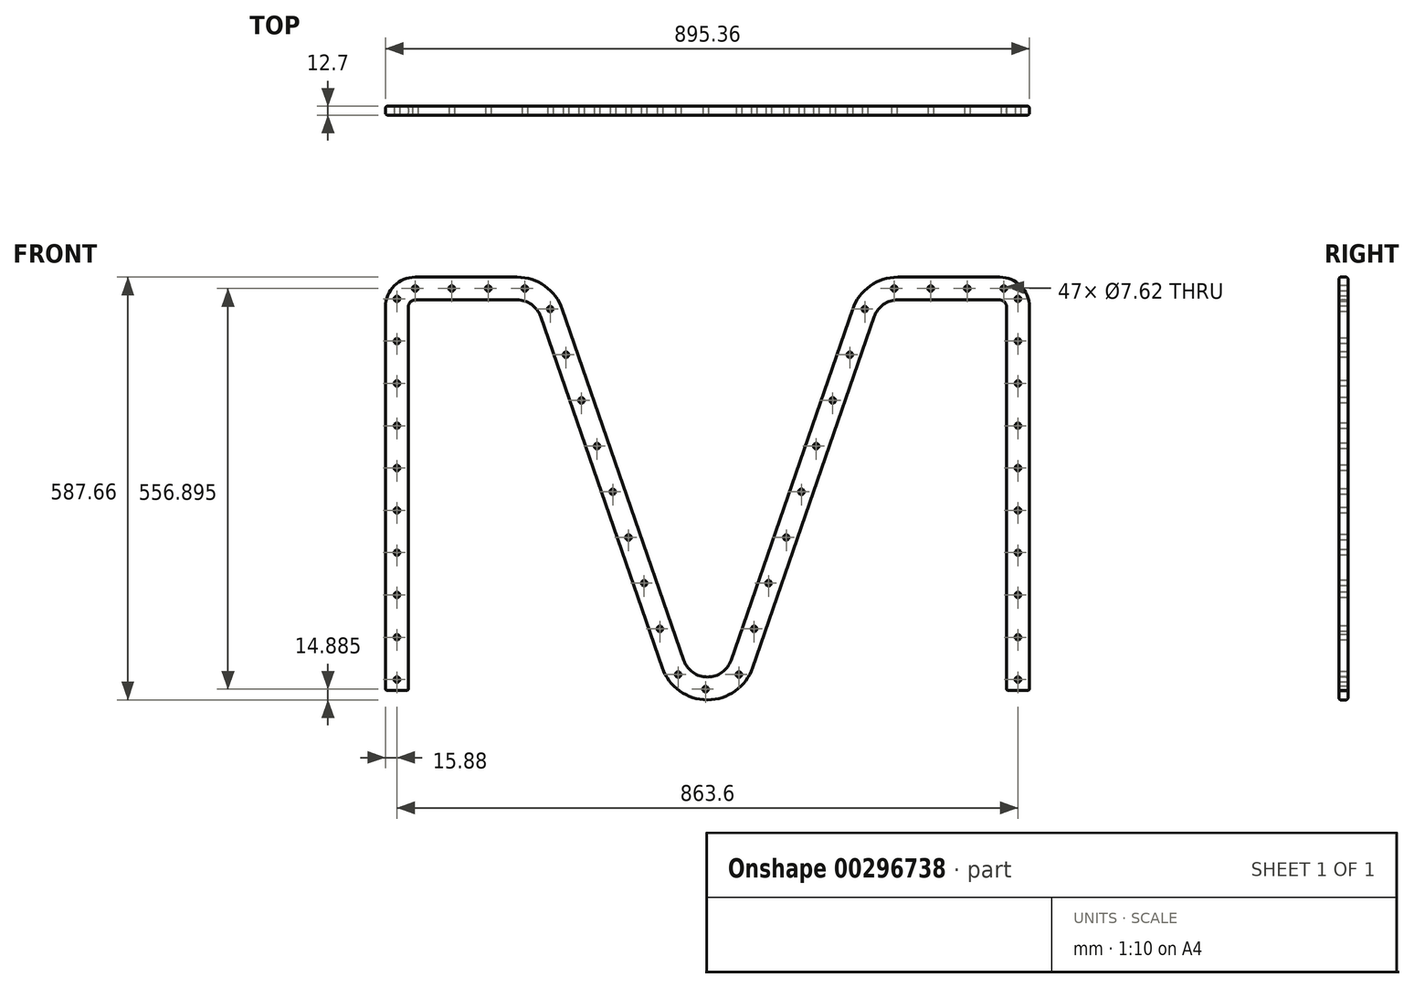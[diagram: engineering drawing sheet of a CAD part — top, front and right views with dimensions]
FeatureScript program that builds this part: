
annotation { "Feature Type Name" : "Feature", "Feature Type Description" : "" }
export const myFeature = defineFeature(function(context is Context, id is Id, definition is map)
    precondition{}
    {
        {
            var Q0;
            Q0=qCreatedBy(makeId("Front.planeOp"),FACE);
            var sketch = newSketch(context, id + "F0", { "sketchPlane" : qUnion([Q0])});
            skLineSegment(sketch, "E0", {"start": v(0, 0) * mm, "end": v(0, 533.4) * mm});
            skLineSegment(sketch, "E1", {"start": v(25.4, 558.8) * mm, "end": v(167.03, 558.8) * mm});
            skLineSegment(sketch, "E2", {"start": v(215.03, 524.62) * mm, "end": v(383.8, 37.08) * mm});
            skLineSegment(sketch, "E3", {"start": v(479.8, 37.08) * mm, "end": v(648.57, 524.62) * mm});
            skLineSegment(sketch, "E4", {"start": v(696.57, 558.8) * mm, "end": v(838.2, 558.8) * mm});
            skLineSegment(sketch, "E5", {"start": v(863.6, 533.4) * mm, "end": v(863.6, 0) * mm});
            skPoint(sketch, "E6.visualSharp", {"position": v(0, 558.8) * mm});
            skArc(sketch, "E6.filletArc", {"start": v(25.4, 558.8) * mm, "mid": v(7.44, 551.36) * mm, "end": v(0, 533.4) * mm});
            skPoint(sketch, "E7.visualSharp", {"position": v(203.2, 558.8) * mm});
            skArc(sketch, "E7.filletArc", {"start": v(215.03, 524.62) * mm, "mid": v(196.5, 549.38) * mm, "end": v(167.03, 558.8) * mm});
            skPoint(sketch, "E8.visualSharp", {"position": v(660.4, 558.8) * mm});
            skArc(sketch, "E8.filletArc", {"start": v(696.57, 558.8) * mm, "mid": v(667.1, 549.38) * mm, "end": v(648.57, 524.62) * mm});
            skPoint(sketch, "E9.visualSharp", {"position": v(431.8, -101.6) * mm});
            skArc(sketch, "E9.filletArc", {"start": v(383.8, 37.08) * mm, "mid": v(431.8, 2.9) * mm, "end": v(479.8, 37.08) * mm});
            skPoint(sketch, "E10.visualSharp", {"position": v(863.6, 558.8) * mm});
            skArc(sketch, "E10.filletArc", {"start": v(863.6, 533.4) * mm, "mid": v(856.16, 551.36) * mm, "end": v(838.2, 558.8) * mm});
            skSolve(sketch);
        }
        {
            var Q0;
            Q0=qCreatedBy(makeId("Top.planeOp"),FACE);
            var sketch = newSketch(context, id + "F1", { "sketchPlane" : qUnion([Q0])});
            skLineSegment(sketch, "E11.bottom", {"start": v(-12.7, 6.35) * mm, "end": v(12.7, 6.35) * mm});
            skLineSegment(sketch, "E11.top", {"start": v(-12.7, -6.35) * mm, "end": v(12.7, -6.35) * mm});
            skLineSegment(sketch, "E11.left", {"start": v(-15.88, 3.18) * mm, "end": v(-15.88, -3.17) * mm});
            skLineSegment(sketch, "E11.right", {"start": v(15.88, 3.18) * mm, "end": v(15.88, -3.17) * mm});
            skPoint(sketch, "E12.visualSharp", {"position": v(-15.88, 6.35) * mm});
            skArc(sketch, "E12.filletArc", {"start": v(-12.7, 6.35) * mm, "mid": v(-14.95, 5.42) * mm, "end": v(-15.88, 3.18) * mm});
            skPoint(sketch, "E13.visualSharp", {"position": v(-15.88, -6.35) * mm});
            skArc(sketch, "E13.filletArc", {"start": v(-15.88, -3.18) * mm, "mid": v(-14.95, -5.42) * mm, "end": v(-12.7, -6.35) * mm});
            skPoint(sketch, "E14.visualSharp", {"position": v(15.88, 6.35) * mm});
            skArc(sketch, "E14.filletArc", {"start": v(15.88, 3.18) * mm, "mid": v(14.95, 5.42) * mm, "end": v(12.7, 6.35) * mm});
            skPoint(sketch, "E15.visualSharp", {"position": v(15.88, -6.35) * mm});
            skArc(sketch, "E15.filletArc", {"start": v(12.7, -6.35) * mm, "mid": v(14.95, -5.42) * mm, "end": v(15.88, -3.17) * mm});
            skSolve(sketch);
        }
        {
            var Q0;
            Q0 = qSketchRegion(id + "F1", true);
            var Q1;
            Q1 = qConstructionFilter(qBodyType(qCreatedBy(id + "F0" ,EDGE), BodyType.WIRE), ConstructionObject.NO);
            sweep(context, id + "F2", {"profiles" : qUnion([Q0]), "path" : qUnion([Q1])});
        }
        {
            var Q0;
            Q0=makeQuery(id+"F2.opSweep","CAP_EDGE",EDGE,{"disambiguationData":[OSD([sQuery(id+"F0.wireOp",VERTEX,"E5.end"),sQuery(id+"F1.wireOp",EDGE,"E11.top")])],"isStart":false});
            fillet(context, id + "F3", {"entities" : qUnion([Q0]), "radius" : 2.54 * mm, "tangentPropagation" : true, "allowEdgeOverflow" : false});
        }
        {
            var Q0;
            Q0=makeQuery(id+"F2.opSweep","CAP_EDGE",EDGE,{"disambiguationData":[OSD([sQuery(id+"F0.wireOp",VERTEX,"E0.start"),sQuery(id+"F1.wireOp",EDGE,"E11.top")])],"isStart":true});
            fillet(context, id + "F4", {"entities" : qUnion([Q0]), "radius" : 2.54 * mm, "tangentPropagation" : true, "allowEdgeOverflow" : false});
        }
        {
            var Q0;
            Q0=makeQuery(id+"F2.opSweep","SWEPT_FACE",FACE,{"disambiguationData":[OSD([sQuery(id+"F0.wireOp",EDGE,"E0"),sQuery(id+"F1.wireOp",EDGE,"E11.top")])]});
            var sketch = newSketch(context, id + "F5", { "sketchPlane" : qUnion([Q0])});
            skCircle(sketch, "E16", {"center": v(0, 15.24) * mm, "radius": 3.81 * mm});
            skPoint(sketch, "E16.centerSnap0", {"position": v(0, 2.54) * mm});
            skCircle(sketch, "E17.0.1.0", {"center": v(0, 74.04) * mm, "radius": 3.81 * mm});
            skCircle(sketch, "E17.0.2.0", {"center": v(0, 132.84) * mm, "radius": 3.81 * mm});
            skCircle(sketch, "E17.0.3.0", {"center": v(0, 191.64) * mm, "radius": 3.81 * mm});
            skCircle(sketch, "E17.0.4.0", {"center": v(0, 250.44) * mm, "radius": 3.81 * mm});
            skCircle(sketch, "E17.0.5.0", {"center": v(0, 309.25) * mm, "radius": 3.81 * mm});
            skCircle(sketch, "E17.0.6.0", {"center": v(0, 368.05) * mm, "radius": 3.81 * mm});
            skCircle(sketch, "E17.0.7.0", {"center": v(0, 426.85) * mm, "radius": 3.81 * mm});
            skCircle(sketch, "E17.0.8.0", {"center": v(0, 485.65) * mm, "radius": 3.81 * mm});
            skCircle(sketch, "E17.0.9.0", {"center": v(0, 544.45) * mm, "radius": 3.81 * mm});
            skLineSegment(sketch, "E17.direction1", {"start": v(0, 15.24) * mm, "end": v(25.4, 15.24) * mm, "construction": true});
            skLineSegment(sketch, "E17.direction2", {"start": v(0, 15.24) * mm, "end": v(0, 74.04) * mm, "construction": true});
            skCircle(sketch, "E18", {"center": v(863.6, 15.24) * mm, "radius": 3.8 * mm});
            skCircle(sketch, "E19.0.1.0", {"center": v(863.6, 74.04) * mm, "radius": 3.8 * mm});
            skCircle(sketch, "E19.0.2.0", {"center": v(863.6, 132.84) * mm, "radius": 3.8 * mm});
            skCircle(sketch, "E19.0.3.0", {"center": v(863.6, 191.64) * mm, "radius": 3.8 * mm});
            skCircle(sketch, "E19.0.4.0", {"center": v(863.6, 250.44) * mm, "radius": 3.8 * mm});
            skCircle(sketch, "E19.0.5.0", {"center": v(863.6, 309.25) * mm, "radius": 3.8 * mm});
            skCircle(sketch, "E19.0.6.0", {"center": v(863.6, 368.05) * mm, "radius": 3.8 * mm});
            skCircle(sketch, "E19.0.7.0", {"center": v(863.6, 426.85) * mm, "radius": 3.8 * mm});
            skCircle(sketch, "E19.0.8.0", {"center": v(863.6, 485.65) * mm, "radius": 3.8 * mm});
            skCircle(sketch, "E19.0.9.0", {"center": v(863.6, 544.45) * mm, "radius": 3.8 * mm});
            skLineSegment(sketch, "E19.direction1", {"start": v(863.6, 15.24) * mm, "end": v(889, 15.24) * mm, "construction": true});
            skLineSegment(sketch, "E19.direction2", {"start": v(863.6, 15.24) * mm, "end": v(863.6, 74.04) * mm, "construction": true});
            skCircle(sketch, "E20", {"center": v(25.4, 558.8) * mm, "radius": 3.81 * mm});
            skCircle(sketch, "E21.1.0.0", {"center": v(76.2, 558.8) * mm, "radius": 3.81 * mm});
            skCircle(sketch, "E21.2.0.0", {"center": v(127, 558.8) * mm, "radius": 3.81 * mm});
            skCircle(sketch, "E21.3.0.0", {"center": v(177.8, 558.8) * mm, "radius": 3.81 * mm});
            skLineSegment(sketch, "E21.direction1", {"start": v(25.4, 558.8) * mm, "end": v(76.2, 558.8) * mm, "construction": true});
            skCircle(sketch, "E22", {"center": v(691.53, 558.8) * mm, "radius": 3.81 * mm});
            skCircle(sketch, "E23.1.0.0", {"center": v(742.33, 558.8) * mm, "radius": 3.81 * mm});
            skCircle(sketch, "E23.2.0.0", {"center": v(793.13, 558.8) * mm, "radius": 3.81 * mm});
            skCircle(sketch, "E23.3.0.0", {"center": v(843.93, 558.8) * mm, "radius": 3.81 * mm});
            skLineSegment(sketch, "E23.direction1", {"start": v(691.53, 558.8) * mm, "end": v(742.33, 558.8) * mm, "construction": true});
            skCircle(sketch, "E24", {"center": v(213.1, 530.23) * mm, "radius": 3.81 * mm});
            skCircle(sketch, "E25", {"center": v(235.07, 466.73) * mm, "radius": 3.81 * mm});
            skCircle(sketch, "E26", {"center": v(256.66, 403.23) * mm, "radius": 3.81 * mm});
            skCircle(sketch, "E27", {"center": v(278.25, 339.73) * mm, "radius": 3.81 * mm});
            skCircle(sketch, "E28", {"center": v(300.1, 276.23) * mm, "radius": 3.81 * mm});
            skCircle(sketch, "E29", {"center": v(321.94, 212.73) * mm, "radius": 3.81 * mm});
            skCircle(sketch, "E30", {"center": v(343.78, 149.23) * mm, "radius": 3.81 * mm});
            skCircle(sketch, "E31", {"center": v(365.63, 85.73) * mm, "radius": 3.81 * mm});
            skCircle(sketch, "E32", {"center": v(391.03, 22.23) * mm, "radius": 3.81 * mm});
            skCircle(sketch, "E33", {"center": v(429.13, 1.9) * mm, "radius": 3.81 * mm});
            skCircle(sketch, "E34", {"center": v(475.6, 22.23) * mm, "radius": 3.8 * mm});
            skCircle(sketch, "E35", {"center": v(496.67, 85.73) * mm, "radius": 3.81 * mm});
            skCircle(sketch, "E36", {"center": v(516.71, 149.23) * mm, "radius": 3.81 * mm});
            skCircle(sketch, "E37", {"center": v(541.39, 212.73) * mm, "radius": 3.81 * mm});
            skCircle(sketch, "E38", {"center": v(562.46, 276.23) * mm, "radius": 3.81 * mm});
            skCircle(sketch, "E39", {"center": v(583.02, 339.73) * mm, "radius": 3.81 * mm});
            skCircle(sketch, "E40", {"center": v(605.97, 403.23) * mm, "radius": 3.81 * mm});
            skCircle(sketch, "E41", {"center": v(629.77, 466.73) * mm, "radius": 3.81 * mm});
            skCircle(sketch, "E42", {"center": v(650.55, 530.23) * mm, "radius": 3.81 * mm});
            skSolve(sketch);
        }
        {
            var Q0;
            Q0 = qSketchRegion(id + "F5", true);
            extrude(context, id + "F6", {"entities" : qUnion([Q0]), "operationType" : NewBodyOperationType.REMOVE, "oppositeDirection" : true, "depth" : 25.4 * mm});
        }
    });
